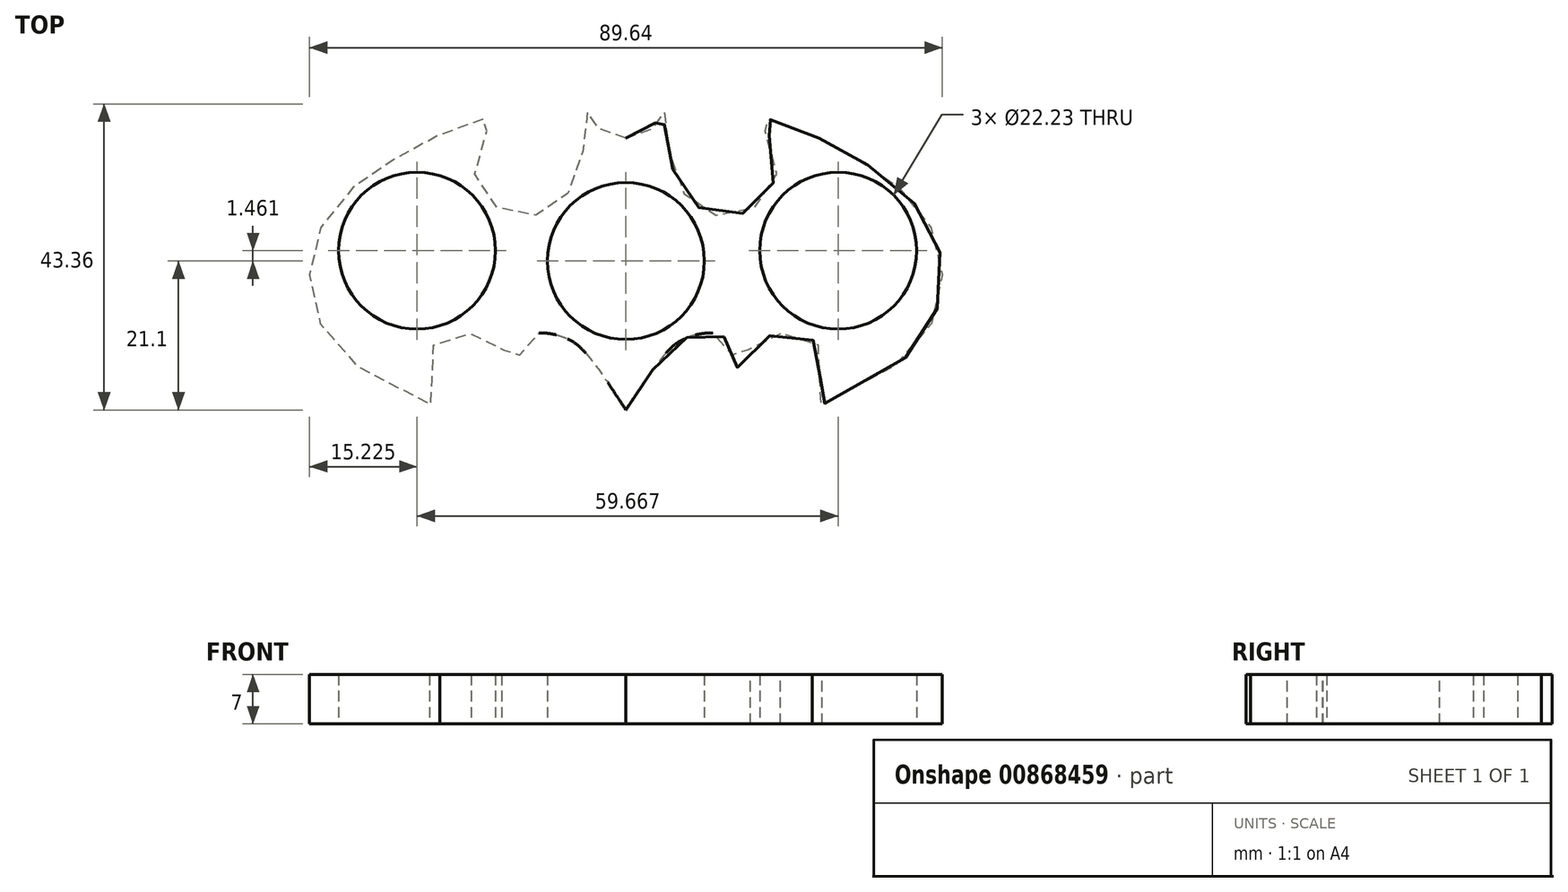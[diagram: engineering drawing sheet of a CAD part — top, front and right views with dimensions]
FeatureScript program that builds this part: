
annotation { "Feature Type Name" : "Feature", "Feature Type Description" : "" }
export const myFeature = defineFeature(function(context is Context, id is Id, definition is map)
    precondition{}
    {
        {
            var Q0;
            Q0=qCreatedBy(makeId("Top.planeOp"),FACE);
            var sketch = newSketch(context, id + "F0", { "sketchPlane" : qUnion([Q0])});
            skCircle(sketch, "E0", {"center": v(0, 0) * mm, "radius": 11.12 * mm});
            skCircle(sketch, "E1", {"center": v(30.07, 1.46) * mm, "radius": 11.12 * mm});
            skCircle(sketch, "E2", {"center": v(-29.6, 1.46) * mm, "radius": 11.12 * mm});
            skFitSpline(sketch, "E3", {"points": [v(0, 17.4) * mm, v(2.48, 17.63) * mm, v(3.92, 18.93) * mm, v(5.32, 22.26) * mm, v(5.48, 19.22) * mm, v(5.96, 16.18) * mm, v(7.24, 11.3) * mm, v(9.48, 8.26) * mm, v(12.68, 6.5) * mm, v(16.76, 6.82) * mm, v(19.48, 8.74) * mm, v(21.4, 12.34) * mm, v(21.3, 16.58) * mm, v(17.63, 20.68) * mm, v(22.92, 19.14) * mm, v(26.6, 17.78) * mm, v(31.24, 15.3) * mm, v(36.52, 12.18) * mm, v(41.64, 7.22) * mm, v(44.2, 2.34) * mm, v(44.76, -3.5) * mm, v(43.16, -9.18) * mm, v(37.88, -15.02) * mm, v(26.52, -20.38) * mm, v(27.04, -18.35) * mm, v(27.75, -14.73) * mm, v(27.36, -12.05) * mm, v(24.08, -10.24) * mm, v(20.62, -10.51) * mm, v(17.7, -12.03) * mm, v(15.5, -15.25) * mm, v(14.83, -11.95) * mm, v(13.51, -10.51) * mm, v(11.4, -10.22) * mm, v(7.96, -11.18) * mm, v(5.16, -13.66) * mm, v(1.96, -18.14) * mm, v(0, -21.1) * mm], "startDerivative": vector(145.36, 1) * mm, "endDerivative": vector(-71.35, -108.17) * mm});
            skFitSpline(sketch, "E4.MirrorCS", {"points": [v(0, 17.4) * mm, v(-2.48, 17.63) * mm, v(-3.92, 18.93) * mm, v(-5.32, 22.26) * mm, v(-5.48, 19.22) * mm, v(-5.96, 16.18) * mm, v(-7.24, 11.3) * mm, v(-9.48, 8.26) * mm, v(-12.68, 6.5) * mm, v(-16.76, 6.82) * mm, v(-19.48, 8.74) * mm, v(-21.4, 12.34) * mm, v(-21.3, 16.58) * mm, v(-17.63, 20.68) * mm, v(-22.92, 19.14) * mm, v(-26.6, 17.78) * mm, v(-31.24, 15.3) * mm, v(-36.52, 12.18) * mm, v(-41.64, 7.22) * mm, v(-44.2, 2.34) * mm, v(-44.76, -3.5) * mm, v(-43.16, -9.18) * mm, v(-37.88, -15.02) * mm, v(-26.52, -20.38) * mm, v(-27.04, -18.35) * mm, v(-27.75, -14.73) * mm, v(-27.36, -12.05) * mm, v(-24.08, -10.24) * mm, v(-20.62, -10.51) * mm, v(-17.7, -12.03) * mm, v(-15.5, -15.25) * mm, v(-14.83, -11.95) * mm, v(-13.51, -10.51) * mm, v(-11.4, -10.22) * mm, v(-7.96, -11.18) * mm, v(-5.16, -13.66) * mm, v(-1.96, -18.14) * mm, v(0, -21.1) * mm], "startDerivative": vector(-145.36, 1) * mm, "endDerivative": vector(71.35, -108.17) * mm});
            skLineSegment(sketch, "E5", {"start": v(-45.41, 29.02) * mm, "end": v(-45.41, -31.4) * mm});
            skLineSegment(sketch, "E6", {"start": v(45.12, 28.82) * mm, "end": v(45.12, -30.8) * mm});
            skLineSegment(sketch, "E7", {"start": v(-45.41, 29.02) * mm, "end": v(45.12, 28.82) * mm});
            skSolve(sketch);
        }
        {
            var Q0;
            Q0=makeQuery(id+"F0.imprint","IMPRINT",FACE,{"disambiguationData":[TD([[makeQuery(id+"F0.imprint","IMPRINT",EDGE,{"derivedFrom":sQuery(id+"F0.wireOp",EDGE,"E0")}),-1.0]])]});
            extrude(context, id + "F1", {"entities" : qUnion([Q0]), "depth" : 7 * mm, "offsetDistance" : 25 * mm});
        }
    });
